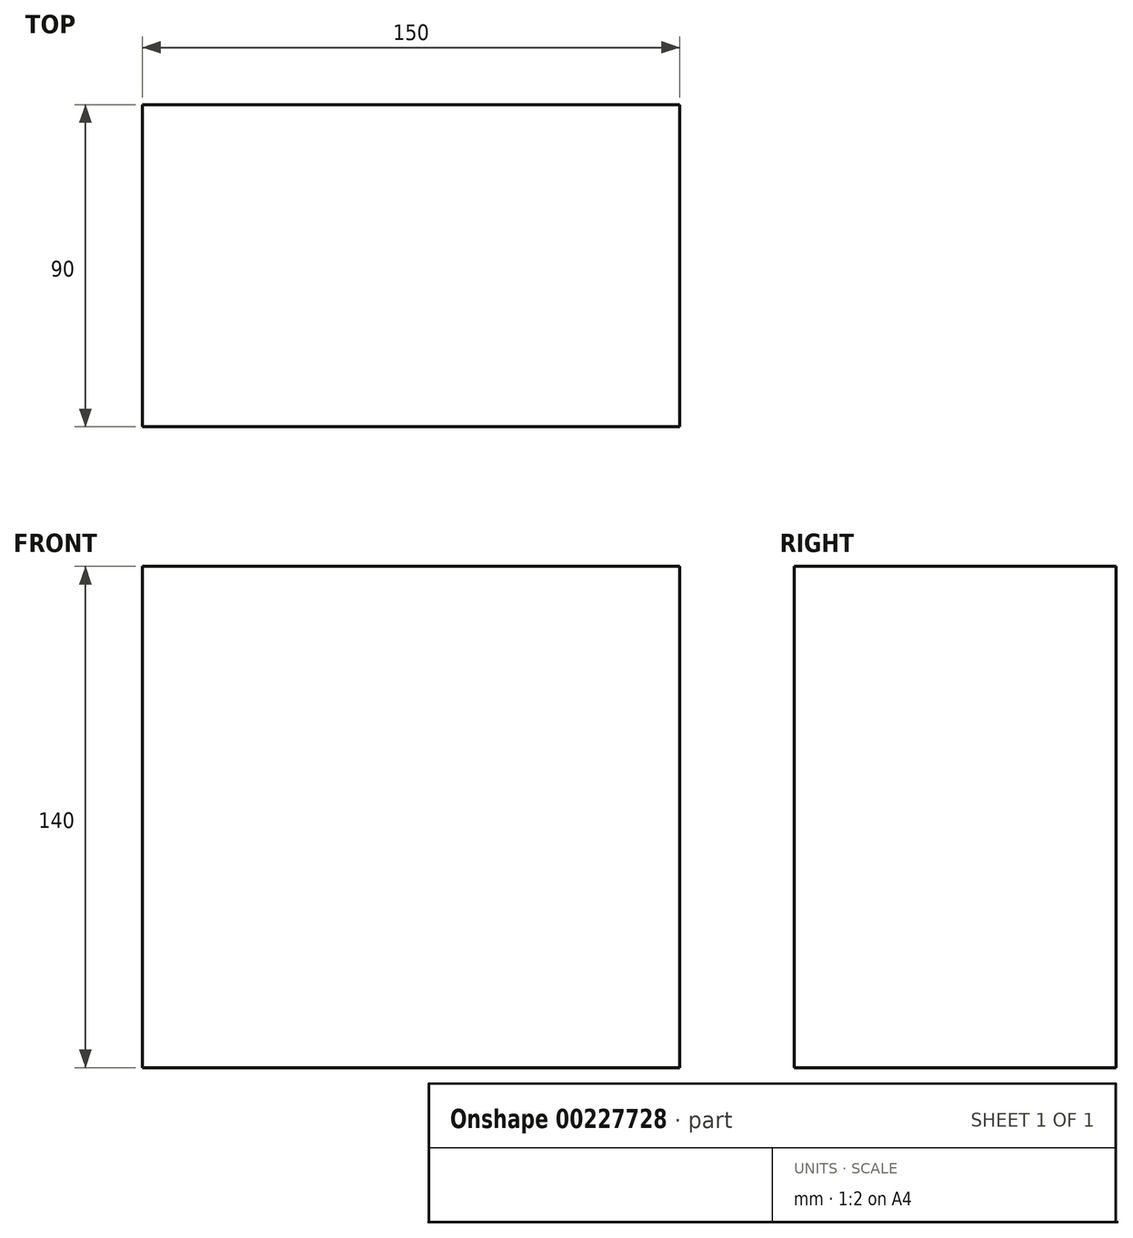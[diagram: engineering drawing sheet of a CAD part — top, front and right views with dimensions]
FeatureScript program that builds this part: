
annotation { "Feature Type Name" : "Feature", "Feature Type Description" : "" }
export const myFeature = defineFeature(function(context is Context, id is Id, definition is map)
    precondition{}
    {
        {
            var Q0;
            Q0=qCreatedBy(makeId("Top.planeOp"),FACE);
            var sketch = newSketch(context, id + "F0", { "sketchPlane" : qUnion([Q0])});
            skLineSegment(sketch, "E0.bottom", {"start": v(75, -45) * mm, "end": v(-75, -45) * mm});
            skLineSegment(sketch, "E0.top", {"start": v(75, 45) * mm, "end": v(-75, 45) * mm});
            skLineSegment(sketch, "E0.left", {"start": v(75, -45) * mm, "end": v(75, 45) * mm});
            skLineSegment(sketch, "E0.right", {"start": v(-75, -45) * mm, "end": v(-75, 45) * mm});
            skPoint(sketch, "E0.middle", {"position": v(0, 0) * mm});
            skSolve(sketch);
        }
        {
            var Q0;
            Q0 = qSketchRegion(id + "F0", true);
            extrude(context, id + "F1", {"entities" : qUnion([Q0]), "depth" : 140 * mm});
        }
    });
